FCSTD DOCUMENT  (FreeCAD 0.18R16110 (Git))
Label: 7sideP
License: All rights reserved
LicenseURL: http://en.wikipedia.org/wiki/All_rights_reserved
objects: Sketcher::SketchObject×1
note: 1 computed .brp shape members not serialized (recipe doc carries the construction recipe); baked Part::Feature solids carry a one-line shape summary decoded from their .brp

FEATURE [Sketcher::SketchObject] Sketch
  sketch-geometry (27):
    g0: LineSegment StartX=-250 StartY=0 StartZ=0 EndX=-155.872 EndY=-195.458 EndZ=0
    g1: LineSegment StartX=-155.872 StartY=-195.458 StartZ=0 EndX=55.6302 EndY=-243.732 EndZ=0
    g2: LineSegment StartX=55.6302 StartY=-243.732 StartZ=0 EndX=225.242 EndY=-108.471 EndZ=0
    g3: LineSegment StartX=225.242 StartY=-108.471 StartZ=0 EndX=225.242 EndY=108.471 EndZ=0
    g4: LineSegment StartX=225.242 StartY=108.471 StartZ=0 EndX=55.6302 EndY=243.732 EndZ=0
    g5: LineSegment StartX=55.6302 StartY=243.732 StartZ=0 EndX=-155.872 EndY=195.458 EndZ=0
    g6: LineSegment StartX=-155.872 StartY=195.458 StartZ=0 EndX=-250 EndY=0 EndZ=0
    g7: Circle [constr] CenterX=0 CenterY=0 CenterZ=0 NormalX=0 NormalY=0 NormalZ=1 AngleXU=0 Radius=250
    g8: LineSegment [constr] StartX=-501.963 StartY=143.293 StartZ=0 EndX=-155.872 EndY=195.458 EndZ=0
    g9: LineSegment [constr] StartX=-198.894 StartY=483.976 StartZ=0 EndX=55.6302 EndY=243.732 EndZ=0
    g10: LineSegment [constr] StartX=253.609 StartY=457.319 StartZ=0 EndX=225.242 EndY=108.471 EndZ=0
    g11: LineSegment [constr] StartX=514.759 StartY=88.2012 StartZ=0 EndX=225.242 EndY=-108.471 EndZ=0
    g12: LineSegment [constr] StartX=55.6302 StartY=-243.732 StartZ=0 EndX=389.363 EndY=-349.196 EndZ=0
    g13: LineSegment [constr] StartX=-423.096 StartY=-304.2 StartZ=0 EndX=-250 EndY=0 EndZ=0
    g14: LineSegment [constr] StartX=-450.335 StartY=151.075 StartZ=0 EndX=-398.894 EndY=-257.892 EndZ=0
    g15: LineSegment [constr] StartX=-398.894 StartY=-257.892 StartZ=0 EndX=-47.0781 EndY=-472.661 EndZ=0
    g16: LineSegment [constr] StartX=-47.0781 StartY=-472.661 StartZ=0 EndX=340.189 EndY=-331.507 EndZ=0
    g17: LineSegment [constr] StartX=340.189 StartY=-331.507 StartZ=0 EndX=471.287 EndY=59.2792 EndZ=0
    g18: LineSegment [constr] StartX=471.287 StartY=59.2792 StartZ=0 EndX=247.496 EndY=405.427 EndZ=0
    g19: LineSegment [constr] StartX=247.496 StartY=405.427 StartZ=0 EndX=-162.664 EndY=446.28 EndZ=0
    g20: LineSegment [constr] StartX=-162.664 StartY=446.28 StartZ=0 EndX=-450.335 EndY=151.075 EndZ=0
    g21: Circle [constr] CenterX=0 CenterY=0 CenterZ=0 NormalX=0 NormalY=0 NormalZ=1 AngleXU=0 Radius=475
    g22: LineSegment [constr] StartX=-155.872 StartY=195.458 StartZ=0 EndX=-19.1135 EndY=216.071 EndZ=0
    g23: LineSegment [constr] StartX=-155.872 StartY=-195.458 StartZ=0 EndX=-28.6451 EndY=-521.515 EndZ=0
    g24: LineSegment [constr] StartX=0 StartY=0 StartZ=0 EndX=-143.09 EndY=-45.0036 EndZ=0
    g25: LineSegment [constr] StartX=0 StartY=0 StartZ=0 EndX=110.519 EndY=-101.418 EndZ=0
    g26: LineSegment [constr] StartX=0 StartY=0 StartZ=0 EndX=32.5706 EndY=146.421 EndZ=0
  constraints (60):
    c: Coincident(g0,g1)
    c: Coincident(g1,g2)
    c: Coincident(g2,g3)
    c: Coincident(g3,g4)
    c: Coincident(g4,g5)
    c: Coincident(g5,g6)
    c: Coincident(g6,g0)
    c: Equal(g0, g1-g6) x6
    c: PointOnObject(g0,g7)
    c: PointOnObject(g1,g7)
    c: PointOnObject(g2,g7)
    c: PointOnObject(g3,g7)
    c: PointOnObject(g4,g7)
    c: PointOnObject(g5,g7)
    c: PointOnObject(g6,g7)
    c: Coincident(g7,g-1)
    c: PointOnObject(g6,g-1)
    c: Radius(g7) = 250
    c: Coincident(g8,g5)
    c: Coincident(g9,g4)
    c: Coincident(g10,g3)
    c: Coincident(g11,g2)
    c: Coincident(g12,g1)
    c: Coincident(g13,g0)
    c: Coincident(g14,g15)
    c: Coincident(g15,g16)
    c: Coincident(g16,g17)
    c: Coincident(g17,g18)
    c: Coincident(g18,g19)
    c: Coincident(g19,g20)
    c: Coincident(g20,g14)
    c: Equal(g14, g15-g20) x6
    c: PointOnObject(g14,g21)
    c: PointOnObject(g15,g21)
    c: PointOnObject(g16,g21)
    c: PointOnObject(g17,g21)
    c: PointOnObject(g18,g21)
    c: PointOnObject(g19,g21)
    c: PointOnObject(g20,g21)
    c: Coincident(g21,g-1)
    c: PointOnObject(g20,g8)
    c: Radius(g21) = 475
    c: Coincident(g22,g5)
    c: Angle(g22,g8) = 3.14159
    c: Coincident(g23,g0)
    c: Equal(g13,g8)
    c: Equal(g8,g9)
    c: Equal(g9,g10)
    c: Equal(g10,g11)
    c: Equal(g11,g12)
    c: Equal(g12,g23)
    c: Distance(g8) = 350
    c: Coincident(g24,g-1)
    c: Coincident(g25,g-1)
    c: Coincident(g26,g-1)
    c: Angle(g24,g25) = 2.0944
    c: Angle(g26,g24) = 2.0944
    c: Equal(g25,g24)
    c: Equal(g24,g26)
    c: Distance(g24) = 150
